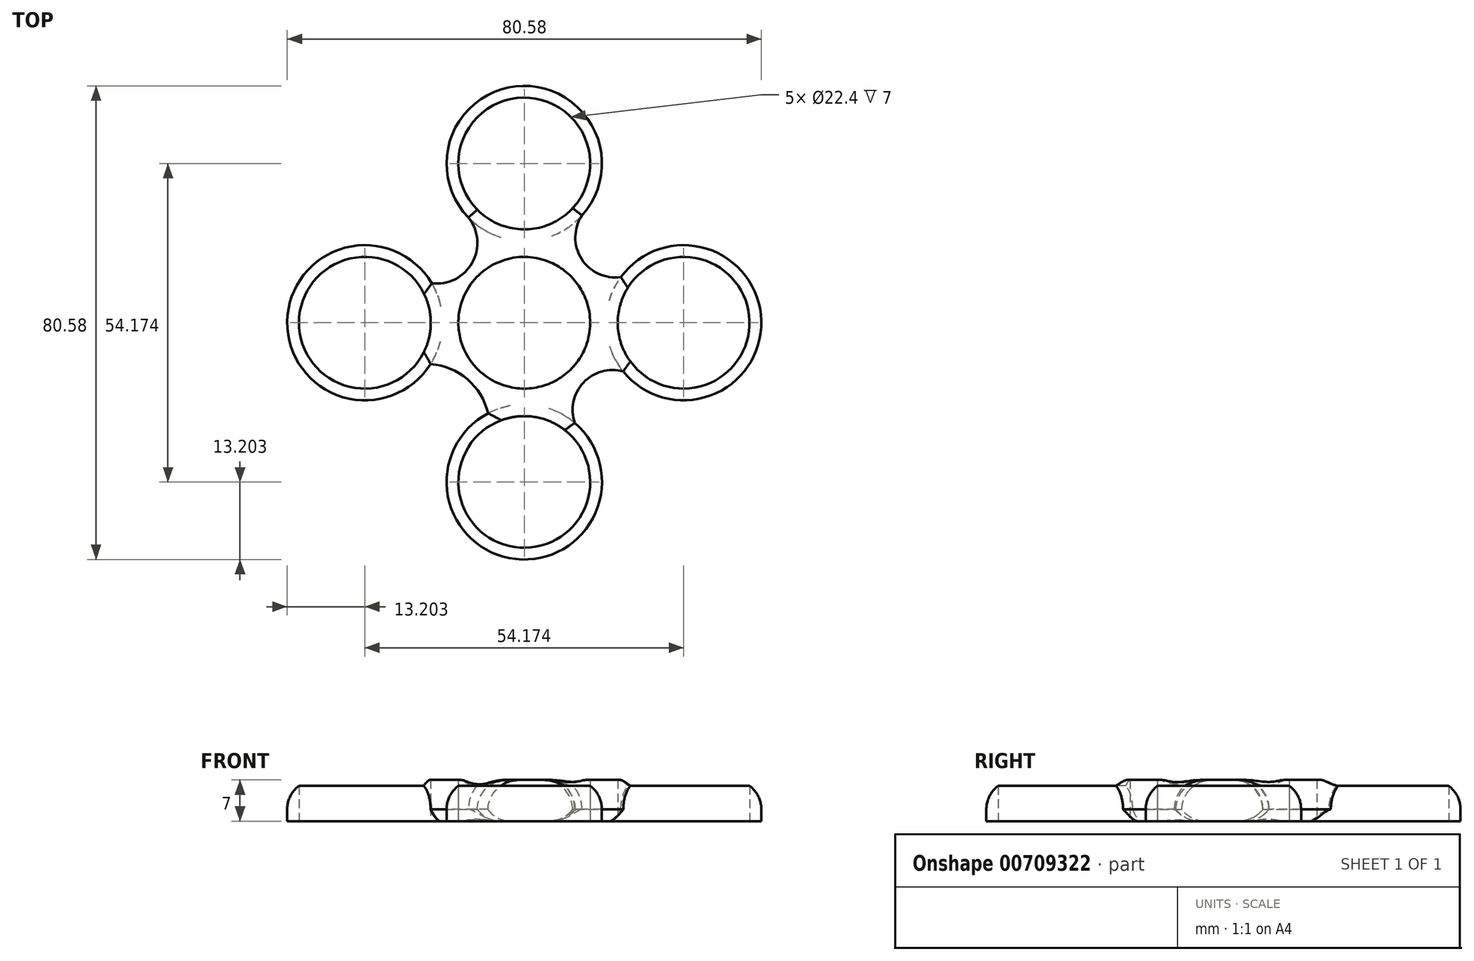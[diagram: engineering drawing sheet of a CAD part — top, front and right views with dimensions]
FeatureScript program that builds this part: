
annotation { "Feature Type Name" : "Feature", "Feature Type Description" : "" }
export const myFeature = defineFeature(function(context is Context, id is Id, definition is map)
    precondition{}
    {
        {
            var Q0;
            Q0=qCreatedBy(makeId("Top.planeOp"),FACE);
            var sketch = newSketch(context, id + "F0", { "sketchPlane" : qUnion([Q0])});
            skCircle(sketch, "E0", {"center": v(0, 0) * mm, "radius": 11.2 * mm});
            skCircle(sketch, "E1", {"center": v(0, 0) * mm, "radius": 13.2 * mm});
            skCircle(sketch, "E2", {"center": v(0, 27.09) * mm, "radius": 11.2 * mm});
            skArc(sketch, "E3", {"start": v(9.8, 18.25) * mm, "mid": v(-0.24, 40.28) * mm, "end": v(-9.48, 17.9) * mm});
            skCircle(sketch, "E4.1.0", {"center": v(-27.09, 0) * mm, "radius": 11.2 * mm});
            skArc(sketch, "E4.1.1", {"start": v(-15.72, 6.72) * mm, "mid": v(-40.29, 0.2) * mm, "end": v(-15.92, -7.04) * mm});
            skCircle(sketch, "E4.2.0", {"center": v(0, -27.09) * mm, "radius": 11.2 * mm});
            skArc(sketch, "E4.2.1", {"start": v(-6.16, -15.41) * mm, "mid": v(-1.46, -40.2) * mm, "end": v(8.58, -17.05) * mm});
            skCircle(sketch, "E4.3.0", {"center": v(27.09, 0) * mm, "radius": 11.2 * mm});
            skArc(sketch, "E4.3.1", {"start": v(16.83, -8.3) * mm, "mid": v(40.28, 0.33) * mm, "end": v(16.42, 7.78) * mm});
            skArc(sketch, "E5", {"start": v(-15.72, 6.72) * mm, "mid": v(-8.64, 10.6) * mm, "end": v(-10.06, 18.54) * mm});
            skArc(sketch, "E6", {"start": v(-6.16, -15.41) * mm, "mid": v(-9.66, -9.61) * mm, "end": v(-15.92, -7.04) * mm});
            skArc(sketch, "E7", {"start": v(16.83, -8.3) * mm, "mid": v(10.05, -10.18) * mm, "end": v(8.58, -17.05) * mm});
            skArc(sketch, "E8", {"start": v(10.64, 19.27) * mm, "mid": v(9.4, 11.45) * mm, "end": v(16.42, 7.78) * mm});
            skSolve(sketch);
        }
        {
            var Q0;
            Q0 = qSketchRegion(id + "F0", true);
            var Q1;
            Q1=makeQuery(id+"F0.imprint","IMPRINT",FACE,{"disambiguationData":[TD([[makeQuery(id+"F0.imprint","IMPRINT",EDGE,{"derivedFrom":sQuery(id+"F0.wireOp",EDGE,"E0")}),-1.0]])]});
            extrude(context, id + "F1", {"entities" : qUnion([Q0, Q1]), "depth" : 7 * mm, "offsetDistance" : 25 * mm});
        }
        {
            var Q0;
            Q0=makeQuery(id+"F1.opExtrude","CAP_EDGE",EDGE,{"disambiguationData":[OSD([sQuery(id+"F0.wireOp",EDGE,"E3")])],"isStart":false});
            var Q1;
            Q1=makeQuery(id+"F1.opExtrude","CAP_EDGE",EDGE,{"disambiguationData":[OSD([sQuery(id+"F0.wireOp",EDGE,"E8")])],"isStart":false});
            var Q2;
            Q2=makeQuery(id+"F1.opExtrude","CAP_EDGE",EDGE,{"disambiguationData":[OSD([sQuery(id+"F0.wireOp",EDGE,"E4.3.1")])],"isStart":false});
            var Q3;
            Q3=makeQuery(id+"F1.opExtrude","CAP_EDGE",EDGE,{"disambiguationData":[OSD([sQuery(id+"F0.wireOp",EDGE,"E7")])],"isStart":false});
            var Q4;
            Q4=makeQuery(id+"F1.opExtrude","CAP_EDGE",EDGE,{"disambiguationData":[OSD([sQuery(id+"F0.wireOp",EDGE,"E4.2.1")])],"isStart":false});
            var Q5;
            Q5=makeQuery(id+"F1.opExtrude","CAP_EDGE",EDGE,{"disambiguationData":[OSD([sQuery(id+"F0.wireOp",EDGE,"E6")])],"isStart":false});
            var Q6;
            Q6=makeQuery(id+"F1.opExtrude","CAP_EDGE",EDGE,{"disambiguationData":[OSD([sQuery(id+"F0.wireOp",EDGE,"E4.1.1")])],"isStart":false});
            var Q7;
            Q7=makeQuery(id+"F1.opExtrude","CAP_EDGE",EDGE,{"disambiguationData":[OSD([sQuery(id+"F0.wireOp",EDGE,"E5")])],"isStart":false});
            fillet(context, id + "F2", {"entities" : qUnion([Q0, Q1, Q2, Q3, Q4, Q5, Q6, Q7]), "radius" : 5 * mm, "tangentPropagation" : true, "allowEdgeOverflow" : false});
        }
        {
            var Q0;
            Q0=makeQuery(id+"F1.opExtrude","CAP_EDGE",EDGE,{"disambiguationData":[OSD([sQuery(id+"F0.wireOp",EDGE,"E5")])],"isStart":true});
            var Q1;
            Q1=makeQuery(id+"F1.opExtrude","CAP_EDGE",EDGE,{"disambiguationData":[OSD([sQuery(id+"F0.wireOp",EDGE,"E6")])],"isStart":true});
            var Q2;
            Q2=makeQuery(id+"F1.opExtrude","CAP_EDGE",EDGE,{"disambiguationData":[OSD([sQuery(id+"F0.wireOp",EDGE,"E7")])],"isStart":true});
            var Q3;
            Q3=makeQuery(id+"F1.opExtrude","CAP_EDGE",EDGE,{"disambiguationData":[OSD([sQuery(id+"F0.wireOp",EDGE,"E8")])],"isStart":true});
            fillet(context, id + "F3", {"entities" : qUnion([Q0, Q1, Q2, Q3]), "radius" : 5 * mm, "tangentPropagation" : true, "allowEdgeOverflow" : false});
        }
    });
